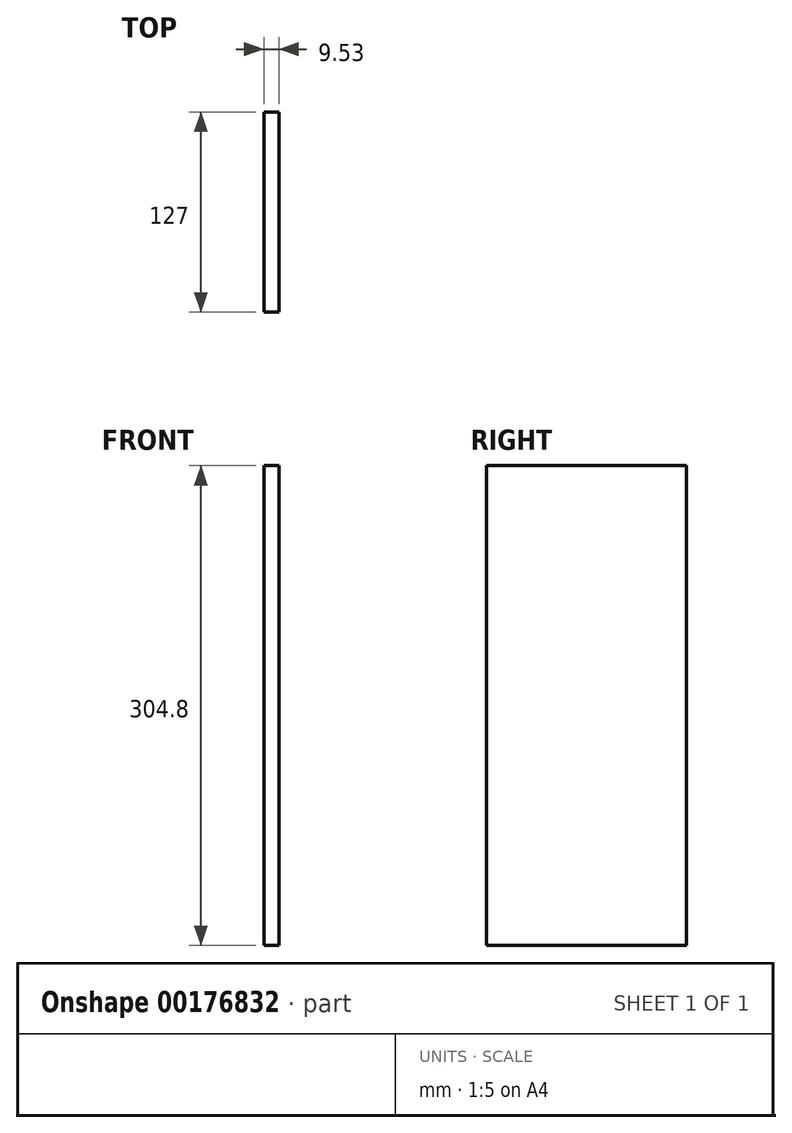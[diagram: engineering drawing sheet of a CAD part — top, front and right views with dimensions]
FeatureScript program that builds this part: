
annotation { "Feature Type Name" : "Feature", "Feature Type Description" : "" }
export const myFeature = defineFeature(function(context is Context, id is Id, definition is map)
    precondition{}
    {
        {
            var Q0;
            Q0=qCreatedBy(makeId("Top.planeOp"),FACE);
            var sketch = newSketch(context, id + "F0", { "sketchPlane" : qUnion([Q0])});
            skLineSegment(sketch, "E0.bottom", {"start": v(-1.52, 89.35) * mm, "end": v(8, 89.35) * mm});
            skLineSegment(sketch, "E0.top", {"start": v(-1.52, -37.65) * mm, "end": v(8, -37.65) * mm});
            skLineSegment(sketch, "E0.left", {"start": v(-1.52, 89.35) * mm, "end": v(-1.52, -37.65) * mm});
            skLineSegment(sketch, "E0.right", {"start": v(8, 89.35) * mm, "end": v(8, -37.65) * mm});
            skSolve(sketch);
        }
        {
            var Q0;
            Q0 = qSketchRegion(id + "F0", true);
            extrude(context, id + "F1", {"entities" : qUnion([Q0]), "depth" : 304.8 * mm});
        }
    });
